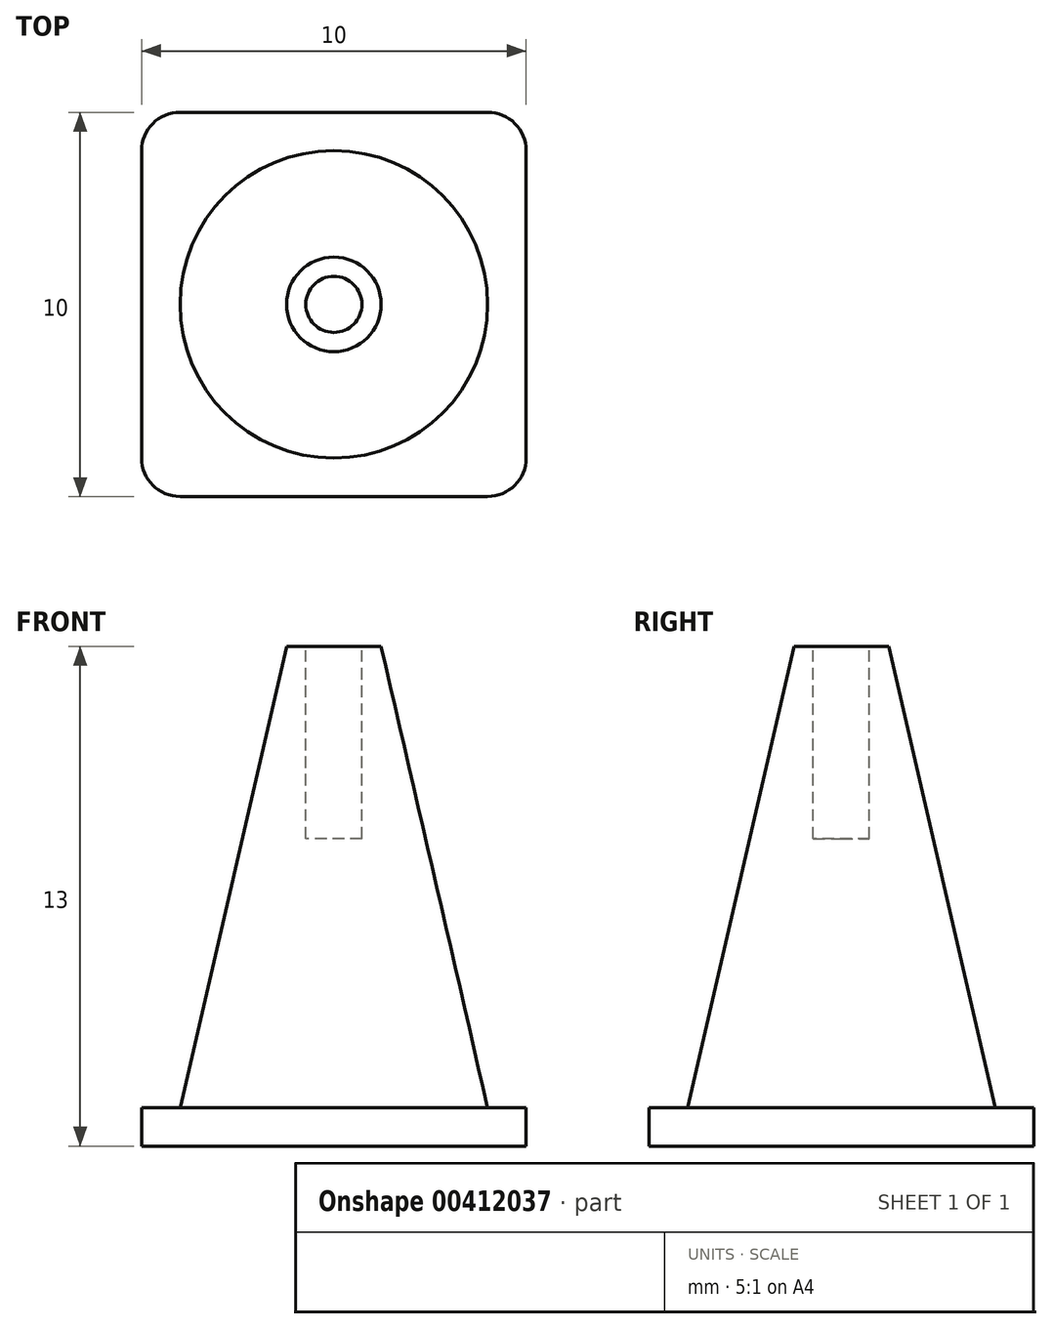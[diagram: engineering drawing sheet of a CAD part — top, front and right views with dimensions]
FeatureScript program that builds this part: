
annotation { "Feature Type Name" : "Feature", "Feature Type Description" : "" }
export const myFeature = defineFeature(function(context is Context, id is Id, definition is map)
    precondition{}
    {
        {
            var Q0;
            Q0=qCreatedBy(makeId("Top.planeOp"),FACE);
            var sketch = newSketch(context, id + "F0", { "sketchPlane" : qUnion([Q0])});
            skLineSegment(sketch, "E0.bottom", {"start": v(1, 0) * mm, "end": v(9, 0) * mm});
            skLineSegment(sketch, "E0.top", {"start": v(1, 10) * mm, "end": v(9, 10) * mm});
            skLineSegment(sketch, "E0.left", {"start": v(0, 1) * mm, "end": v(0, 9) * mm});
            skLineSegment(sketch, "E0.right", {"start": v(10, 1) * mm, "end": v(10, 9) * mm});
            skPoint(sketch, "E1.visualSharp", {"position": v(0, 10) * mm});
            skArc(sketch, "E1.filletArc", {"start": v(1, 10) * mm, "mid": v(0.3, 9.7) * mm, "end": v(0, 9) * mm});
            skPoint(sketch, "E2.visualSharp", {"position": v(10, 10) * mm});
            skArc(sketch, "E2.filletArc", {"start": v(10, 9) * mm, "mid": v(9.7, 9.7) * mm, "end": v(9, 10) * mm});
            skPoint(sketch, "E3.visualSharp", {"position": v(10, 0) * mm});
            skArc(sketch, "E3.filletArc", {"start": v(9, 0) * mm, "mid": v(9.7, 0.3) * mm, "end": v(10, 1) * mm});
            skPoint(sketch, "E4.visualSharp", {"position": v(0, 0) * mm});
            skArc(sketch, "E4.filletArc", {"start": v(0, 1) * mm, "mid": v(0.3, 0.3) * mm, "end": v(1, 0) * mm});
            skSolve(sketch);
        }
        {
            var Q0;
            Q0 = qSketchRegion(id + "F0", true);
            extrude(context, id + "F1", {"entities" : qUnion([Q0]), "depth" : 1 * mm});
        }
        {
            var Q0;
            Q0=makeQuery(id+"F1.opExtrude","CAP_FACE",FACE,{"disambiguationData":[OSD([sQuery(id+"F0.wireOp",EDGE,"E0.bottom"),sQuery(id+"F0.wireOp",EDGE,"E0.top"),sQuery(id+"F0.wireOp",EDGE,"E0.left"),sQuery(id+"F0.wireOp",EDGE,"E0.right"),sQuery(id+"F0.wireOp",EDGE,"E1.filletArc"),sQuery(id+"F0.wireOp",EDGE,"E2.filletArc"),sQuery(id+"F0.wireOp",EDGE,"E3.filletArc"),sQuery(id+"F0.wireOp",EDGE,"E4.filletArc")])],"isStart":false});
            var sketch = newSketch(context, id + "F2", { "sketchPlane" : qUnion([Q0])});
            skCircle(sketch, "E5", {"center": v(5, 5) * mm, "radius": 4 * mm});
            skPoint(sketch, "E5.centerSnap0", {"position": v(0, 5) * mm});
            skPoint(sketch, "E5.centerSnap1", {"position": v(5, 10) * mm});
            skSolve(sketch);
        }
        {
            var Q0;
            Q0 = qSketchRegion(id + "F2", true);
            extrude(context, id + "F3", {"entities" : qUnion([Q0]), "operationType" : NewBodyOperationType.ADD, "depth" : 12 * mm, "hasDraft" : true, "draftAngle" : 13 * degree, "draftPullDirection" : true});
        }
        {
            var Q0;
            Q0=makeQuery(id+"F3.opExtrude","CAP_FACE",FACE,{"disambiguationData":[OSD([sQuery(id+"F2.wireOp",EDGE,"E5")])],"isStart":false});
            var sketch = newSketch(context, id + "F4", { "sketchPlane" : qUnion([Q0])});
            skCircle(sketch, "E6", {"center": v(5, 5) * mm, "radius": 0.73 * mm});
            skSolve(sketch);
        }
        {
            var Q0;
            Q0=makeQuery(id+"F4.imprint","IMPRINT",FACE,{"disambiguationData":[TD([[makeQuery(id+"F4.imprint","IMPRINT",EDGE,{"derivedFrom":sQuery(id+"F4.wireOp",EDGE,"E6")}),1.0]])]});
            var Q1;
            Q1=sQuery(id+"F4.wireOp",EDGE,"E6");
            extrude(context, id + "F5", {"entities" : qUnion([Q0]), "operationType" : NewBodyOperationType.REMOVE, "surfaceEntities" : qUnion([Q1]), "oppositeDirection" : true, "depth" : 5 * mm});
        }
    });
